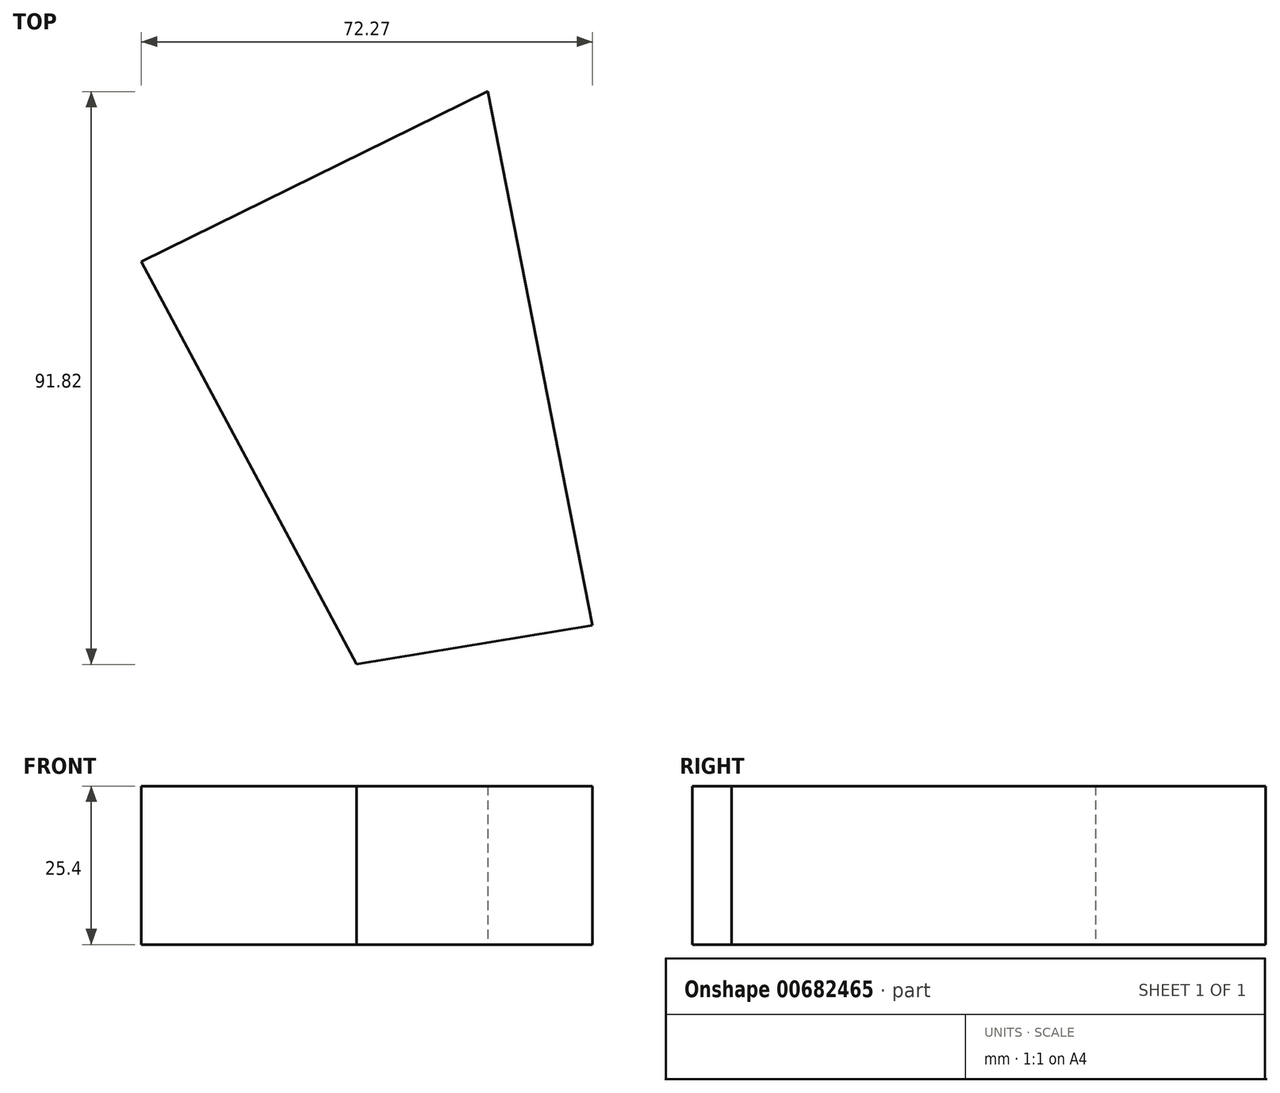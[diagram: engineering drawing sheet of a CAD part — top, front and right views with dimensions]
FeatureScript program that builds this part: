
annotation { "Feature Type Name" : "Feature", "Feature Type Description" : "" }
export const myFeature = defineFeature(function(context is Context, id is Id, definition is map)
    precondition{}
    {
        {
            var Q0;
            Q0=qCreatedBy(makeId("Top.planeOp"),FACE);
            var sketch = newSketch(context, id + "F0", { "sketchPlane" : qUnion([Q0])});
            skLineSegment(sketch, "E0", {"start": v(-41.8, 40.7) * mm, "end": v(-41.8, -37.03) * mm});
            skLineSegment(sketch, "E1", {"start": v(-41.8, -37.03) * mm, "end": v(27.5, -37.03) * mm});
            skLineSegment(sketch, "E2", {"start": v(27.5, -37.03) * mm, "end": v(38.86, -37.03) * mm});
            skLineSegment(sketch, "E3", {"start": v(38.86, -37.03) * mm, "end": v(58.3, -55.36) * mm});
            skLineSegment(sketch, "E4", {"start": v(58.3, -55.36) * mm, "end": v(58.3, 43.26) * mm});
            skLineSegment(sketch, "E5", {"start": v(58.3, 43.26) * mm, "end": v(-41.8, 40.7) * mm});
            skSolve(sketch);
        }
        {
            var Q0;
            Q0=sQuery(id+"F0.wireOp",EDGE,"E4");
            var Q1;
            Q1=sQuery(id+"F0.wireOp",EDGE,"E3");
            var Q2;
            Q2=sQuery(id+"F0.wireOp",EDGE,"E5");
            var Q3;
            Q3=sQuery(id+"F0.wireOp",EDGE,"E2");
            var Q4;
            Q4=sQuery(id+"F0.wireOp",EDGE,"E1");
            var Q5;
            Q5=sQuery(id+"F0.wireOp",EDGE,"E0");
            extrude(context, id + "F1", {"bodyType" : ToolBodyType.SURFACE, "surfaceEntities" : qUnion([Q0, Q1, Q2, Q3, Q4, Q5]), "depth" : 76.5 * mm, "offsetDistance" : 25.4 * mm});
        }
        {
            var Q0;
            Q0=qCreatedBy(makeId("Top.planeOp"),FACE);
            var sketch = newSketch(context, id + "F2", { "sketchPlane" : qUnion([Q0])});
            skLineSegment(sketch, "E6", {"start": v(48.06, 51) * mm, "end": v(-55.76, 0) * mm});
            skLineSegment(sketch, "E7", {"start": v(-55.76, 0) * mm, "end": v(-21.28, -64.57) * mm});
            skLineSegment(sketch, "E8", {"start": v(-21.28, -64.57) * mm, "end": v(16.5, -58.33) * mm});
            skLineSegment(sketch, "E9", {"start": v(16.5, -58.33) * mm, "end": v(-5.5, 53.93) * mm});
            skSolve(sketch);
        }
        {
            var Q0;
            Q0 = qSketchRegion(id + "F2", true);
            var Q1;
            {var subQ0=sQuery(id+"F2.wireOp",EDGE,"E7");Q1=makeQuery(id+"F2.imprint","IMPRINT",FACE,{"disambiguationData":[TD([[makeQuery(id+"F2.imprint","IMPRINT",EDGE,{"derivedFrom":subQ0}),1.0]])]});}
            extrude(context, id + "F3", {"entities" : qUnion([Q0, Q1]), "depth" : 25.4 * mm, "offsetDistance" : 25.4 * mm});
        }
    });
